# Revit family: Hand_Dryer-Excel_Dryer-XLERATOReco_Unit
name_source: partatom
category: Specialty Equipment
revit_build: Autodesk Revit 2015 (Build: 20140606_1530(x64)
units: mm (PartAtom-declared; Revit-internal decimal feet)

## types (1)
- Not a Type - Load Type Catalog
    ADA Compliance = http://www.exceldryer.com
    Amperage = 0 A
    Apparent Load = 500 VA
    Assembly Code = C1030200
    Category = Toilet Accessories
    Cost Information = http://www.exceldryer.com
    Cost Savings Analysis = http://www.exceldryer.com
    Cover Finish = Bulk Molding Compound -  Excel Dryer - Thermoset Resin - White
    Cover Material = Thermoset BMC
    Default Elevation = 3' - 5"
    Depth = 0' - 6 7/8"
    Description = XLERATOReco Hand Dryer
    Dry Time = 10-15 Seconds
    Expected Lifespan = 15+ Years
    Frequency = 60 Hz
    Green Building LEED = http://www.exceldryer.com
    Height = 1' - 0 7/8"
    Impact Resistant Note = UL 499
    Installation Phase = Single
    Installation URL = http://www.exceldryer.com
    Maintenance Schedule = Once to Twice per Year
    Manufacturer = Excel Dryer
    Manufacturer Fax = 1-413-525-2853
    Manufacturer Toll Free Number = 800-255-9235
    Model = Wall Guard White
    Motor Note = 2-4.5 Amps
    Number of Poles = 1
    Output at Outlet (LFM) = 16000
    Phase = 1
    Power Factor = 1
    Product Documentation Link = http://www.exceldryer.com
    Product Name = XLERATOReco Hand Dryer
    Product Page URL = http://www.exceldryer.com
    Product Weight = 17lbs
    Product data url = https://bimobject.com
    Run-Time Cycle = Automatic
    Subcategory = Hand Dryers
    Time Cycle = Automatic
    URL = http://www.exceldryer.com
    Void = 0' - 0 1/16"
    Void Depth = 6' - 7 15/16"
    Voltage = 120 V
    Warranty Duration = 5 Years
    Warranty URL = http://www.exceldryer.com
    Watts = 500 W
    Width = 0' - 11 15/16"
    ecoScorecard Product Page = http://exceldryer.ecoscorecard.com

## geometry (parser evidence)
native form markers: Blend x12, Sweep x2
no freeform markers — native parametric forms only
